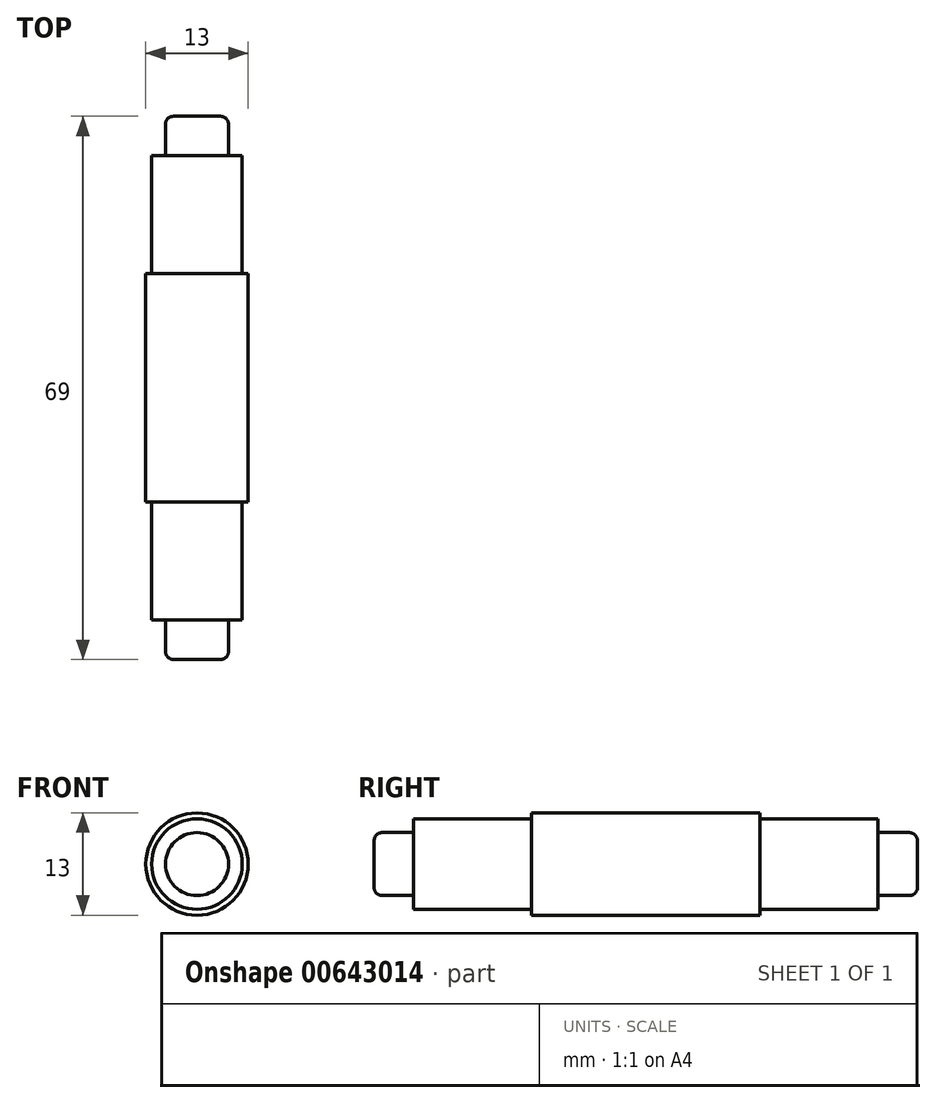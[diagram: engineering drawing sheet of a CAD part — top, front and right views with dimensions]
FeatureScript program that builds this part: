
annotation { "Feature Type Name" : "Feature", "Feature Type Description" : "" }
export const myFeature = defineFeature(function(context is Context, id is Id, definition is map)
    precondition{}
    {
        {
            var Q0;
            Q0=qCreatedBy(makeId("Front.planeOp"),FACE);
            var sketch = newSketch(context, id + "F0", { "sketchPlane" : qUnion([Q0])});
            skCircle(sketch, "E0", {"center": v(0, 0) * mm, "radius": 6.5 * mm});
            skSolve(sketch);
        }
        {
            var Q0;
            Q0 = qSketchRegion(id + "F0", true);
            extrude(context, id + "F1", {"entities" : qUnion([Q0]), "depth" : 29 * mm, "offsetDistance" : 25 * mm});
        }
        {
            var Q0;
            Q0=qCreatedBy(makeId("Front.planeOp"),FACE);
            var sketch = newSketch(context, id + "F2", { "sketchPlane" : qUnion([Q0])});
            skCircle(sketch, "E1", {"center": v(0, 0) * mm, "radius": 5.75 * mm});
            skSolve(sketch);
        }
        {
            var Q0;
            Q0=makeQuery(id+"F2.imprint","IMPRINT",FACE,{"disambiguationData":[TD([[makeQuery(id+"F2.imprint","IMPRINT",EDGE,{"derivedFrom":sQuery(id+"F2.wireOp",EDGE,"E1")}),1.0]])]});
            extrude(context, id + "F3", {"entities" : qUnion([Q0]), "operationType" : NewBodyOperationType.ADD, "oppositeDirection" : true, "depth" : 15 * mm, "offsetDistance" : 25 * mm});
        }
        {
            var Q0;
            Q0=makeQuery(id+"F3.opExtrude","CAP_FACE",FACE,{"disambiguationData":[OSD([sQuery(id+"F2.wireOp",EDGE,"E1")])],"isStart":false});
            var sketch = newSketch(context, id + "F4", { "sketchPlane" : qUnion([Q0])});
            skCircle(sketch, "E2", {"center": v(0, 0) * mm, "radius": 4 * mm});
            skSolve(sketch);
        }
        {
            var Q0;
            Q0=makeQuery(id+"F4.imprint","IMPRINT",FACE,{"disambiguationData":[TD([[makeQuery(id+"F4.imprint","IMPRINT",EDGE,{"derivedFrom":sQuery(id+"F4.wireOp",EDGE,"E2")}),1.0]])]});
            extrude(context, id + "F5", {"entities" : qUnion([Q0]), "operationType" : NewBodyOperationType.ADD, "depth" : 5 * mm, "offsetDistance" : 25 * mm});
        }
        {
            var Q0;
            Q0=makeQuery(id+"F1.opExtrude","CAP_FACE",FACE,{"disambiguationData":[OSD([sQuery(id+"F0.wireOp",EDGE,"E0")])],"isStart":false});
            var sketch = newSketch(context, id + "F6", { "sketchPlane" : qUnion([Q0])});
            skCircle(sketch, "E3", {"center": v(0, 0) * mm, "radius": 5.75 * mm});
            skSolve(sketch);
        }
        {
            var Q0;
            Q0=makeQuery(id+"F6.imprint","IMPRINT",FACE,{"disambiguationData":[TD([[makeQuery(id+"F6.imprint","IMPRINT",EDGE,{"derivedFrom":sQuery(id+"F6.wireOp",EDGE,"E3")}),1.0]])]});
            extrude(context, id + "F7", {"entities" : qUnion([Q0]), "operationType" : NewBodyOperationType.ADD, "depth" : 15 * mm, "offsetDistance" : 25 * mm});
        }
        {
            var Q0;
            Q0=makeQuery(id+"F7.opExtrude","CAP_FACE",FACE,{"disambiguationData":[OSD([sQuery(id+"F6.wireOp",EDGE,"E3")])],"isStart":false});
            var sketch = newSketch(context, id + "F8", { "sketchPlane" : qUnion([Q0])});
            skCircle(sketch, "E4", {"center": v(0, 0) * mm, "radius": 4 * mm});
            skSolve(sketch);
        }
        {
            var Q0;
            Q0=makeQuery(id+"F8.imprint","IMPRINT",FACE,{"disambiguationData":[TD([[makeQuery(id+"F8.imprint","IMPRINT",EDGE,{"derivedFrom":sQuery(id+"F8.wireOp",EDGE,"E4")}),1.0]])]});
            extrude(context, id + "F9", {"entities" : qUnion([Q0]), "operationType" : NewBodyOperationType.ADD, "depth" : 5 * mm, "offsetDistance" : 25 * mm});
        }
        {
            var Q0;
            Q0=makeQuery(id+"F9.opExtrude","CAP_EDGE",EDGE,{"disambiguationData":[OSD([sQuery(id+"F8.wireOp",EDGE,"E4")])],"isStart":false});
            var Q1;
            Q1=makeQuery(id+"F5.opExtrude","CAP_EDGE",EDGE,{"disambiguationData":[OSD([sQuery(id+"F4.wireOp",EDGE,"E2")])],"isStart":false});
            fillet(context, id + "F10", {"entities" : qUnion([Q0, Q1]), "radius" : 1 * mm, "tangentPropagation" : true, "allowEdgeOverflow" : false});
        }
    });
